# Revit family: RollHolder-Vitra-İstanbulSeries-A48016
name_source: partatom
category: Plumbing Fixtures
revit_build: Autodesk Revit 2017 (Build: 20160225_1515(x64)
units: mm (PartAtom-declared; Revit-internal decimal feet)

## family parameters
Cut with Voids When Loaded = No
Host = Face
OmniClass Number = 23.45.05.14.99
OmniClass Title = Other Sanitary Washing Plumbing Fixtures
Part Type = Normal
Room Calculation Point = No
Round Connector Dimension = Use Diameter
Shared = Yes

## types (2) — shared parameters
BIMobject category = Sanitary - Bathroom Accessories
CW Connection = No
Depth(mm) = 132 mm
Description = Istanbul Roll Holder - Double
Design country = Turkey
HW Connection = No
Height(mm) = 132 mm
IFC Classification = Sanitary Terminal
Installation instructions = https://cdn.vitra.com.tr
Manufacturer = Vitra
Manufacturer name = Vitra
MountingType = Wall-mounted
NBS Referans Code = 35-75-88
NBS Referans Description = Toilet Roll Holders
Nominal height = 0.000
Nominal width = 0.000
OmniClass Code = 23-31 25 00
OmniClass Description = Toilet and Bath Specialties
Product Type = Built-in Roll Holder
Product certification = https://vitraglobal.com
Product data url = https://www.vitraglobal.com
Product family = İstanbulSeries
Product group = Roll Holder
Technical description = https://www.vitraglobal.com
URL = https://vitraglobal.com
Uniclass 1.4 Code = L7313
Uniclass 1.4 Description = Sanitary above ground pipes and fittings
Uniclass 2.0 Code = PR-35-75-88
Uniclass 2.0 Description = Toilet Roll Holders
Uniclass 2015 Code = Pr_40_20_76_88
Uniclass 2015 Name = Toilet roll holders
Uniformat II Description = FURNISHINGS
Vent Connection = No
Warranty Period (Year) = 5 years
Waste Connection = No
Weight Net (kg) = 2,700
Width(mm) = 345 mm  [stored 1.13189 ft]
Youtube = https://www.youtube.com
zero-valued in all types: CWFU, Cost, Default Elevation, HWFU, WFU

## per-type parameters (varying)
| type | Article No. (default) | Coating Material | Color | Model | Product SKU |
| RollHolder-Vitra-İstanbulSeries(Chrome)-A48016 | A48016 | Vitra-Chrome | Chrome | A48016 | A48016 |
| RollHolder-Vitra-İstanbulSeries(Gold)-A4801623 | A4801623 | Vitra-Gold | Gold | A4801623 | A4801623 |

note: [stored X ft] marks values corroborated as IEEE doubles in the binary element streams (Revit-internal decimal feet)

## geometry (parser evidence)
native form markers: Sweep x3
no freeform markers — native parametric forms only
